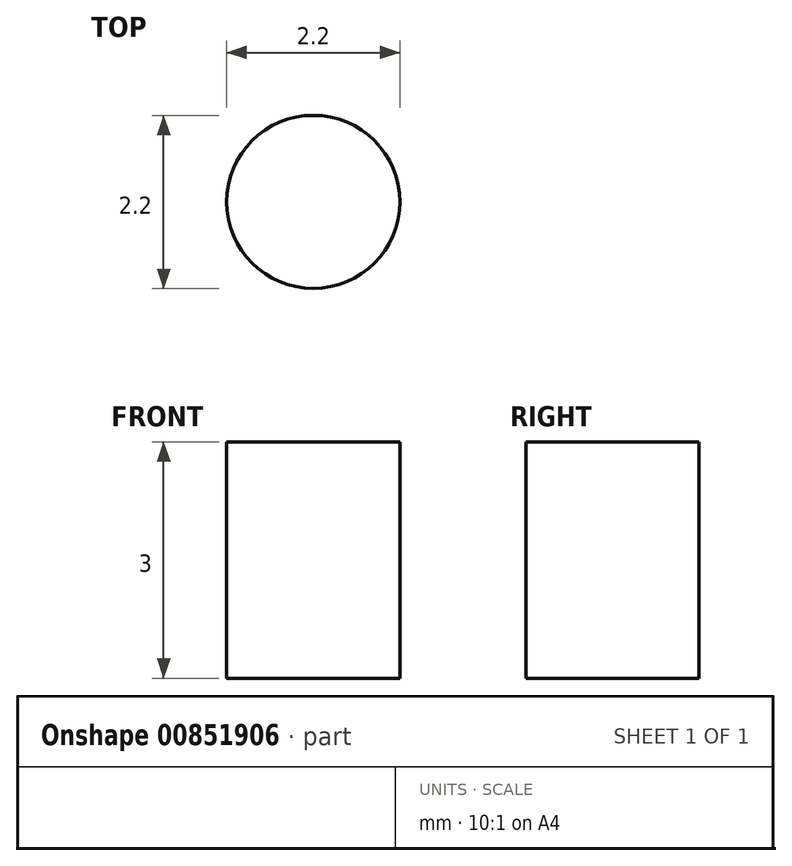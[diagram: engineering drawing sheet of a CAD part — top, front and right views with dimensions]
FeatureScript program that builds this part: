
annotation { "Feature Type Name" : "Feature", "Feature Type Description" : "" }
export const myFeature = defineFeature(function(context is Context, id is Id, definition is map)
    precondition{}
    {
        {
            var Q0;
            Q0=qCreatedBy(makeId("Top.planeOp"),FACE);
            var sketch = newSketch(context, id + "F0", { "sketchPlane" : qUnion([Q0])});
            skLineSegment(sketch, "E0.bottom", {"start": v(0, 0) * mm, "end": v(297, 0) * mm, "construction": true});
            skLineSegment(sketch, "E0.top", {"start": v(0, 210) * mm, "end": v(297, 210) * mm, "construction": true});
            skLineSegment(sketch, "E0.left", {"start": v(0, 0) * mm, "end": v(0, 210) * mm, "construction": true});
            skLineSegment(sketch, "E0.right", {"start": v(297, 0) * mm, "end": v(297, 210) * mm, "construction": true});
            skCircle(sketch, "E1.MirrorC", {"center": v(268.86, 107.9) * mm, "radius": 1.1 * mm});
            skCircle(sketch, "E2.MirrorC", {"center": v(181.7, 17) * mm, "radius": 1.1 * mm});
            skCircle(sketch, "E3.MirrorC", {"center": v(31.1, 63.5) * mm, "radius": 1.1 * mm});
            skCircle(sketch, "E4.MirrorC", {"center": v(270.3, 149.4) * mm, "radius": 1.1 * mm});
            skCircle(sketch, "E5.MirrorC", {"center": v(179.5, 167.6) * mm, "radius": 1.1 * mm});
            skCircle(sketch, "E6.MirrorC", {"center": v(35.2, 173) * mm, "radius": 1.1 * mm});
            skCircle(sketch, "E7.MirrorC", {"center": v(132.2, 155.5) * mm, "radius": 1.1 * mm});
            skCircle(sketch, "E8.MirrorC", {"center": v(132.2, 92.5) * mm, "radius": 1.1 * mm});
            skCircle(sketch, "E9.MirrorC", {"center": v(31.1, 100) * mm, "radius": 1.1 * mm});
            skCircle(sketch, "E10.MirrorC", {"center": v(85.7, 17) * mm, "radius": 1.1 * mm});
            skCircle(sketch, "E11.MirrorC", {"center": v(24.2, 17) * mm, "radius": 1.1 * mm});
            skLineSegment(sketch, "E12.MirrorCS", {"start": v(293, 190) * mm, "end": v(293, 6) * mm});
            skLineSegment(sketch, "E13.MirrorCS", {"start": v(292, 5) * mm, "end": v(6, 5) * mm});
            skLineSegment(sketch, "E14.MirrorCS", {"start": v(5, 6) * mm, "end": v(5, 190) * mm});
            skLineSegment(sketch, "E15.MirrorCS", {"start": v(6, 191) * mm, "end": v(292, 191) * mm});
            skLineSegment(sketch, "E16.bottom", {"start": v(18, 11) * mm, "end": v(28, 11) * mm});
            skLineSegment(sketch, "E16.top", {"start": v(18, 8) * mm, "end": v(28, 8) * mm});
            skLineSegment(sketch, "E16.left", {"start": v(18, 11) * mm, "end": v(18, 8) * mm});
            skLineSegment(sketch, "E16.right", {"start": v(28, 11) * mm, "end": v(28, 8) * mm});
            skLineSegment(sketch, "E17.bottom", {"start": v(102, 11) * mm, "end": v(112, 11) * mm});
            skLineSegment(sketch, "E17.top", {"start": v(102, 8) * mm, "end": v(112, 8) * mm});
            skLineSegment(sketch, "E17.left", {"start": v(102, 11) * mm, "end": v(102, 8) * mm});
            skLineSegment(sketch, "E17.right", {"start": v(112, 11) * mm, "end": v(112, 8) * mm});
            skLineSegment(sketch, "E18.bottom", {"start": v(8, 28) * mm, "end": v(11, 28) * mm});
            skLineSegment(sketch, "E18.top", {"start": v(8, 18) * mm, "end": v(11, 18) * mm});
            skLineSegment(sketch, "E18.left", {"start": v(8, 28) * mm, "end": v(8, 18) * mm});
            skLineSegment(sketch, "E18.right", {"start": v(11, 28) * mm, "end": v(11, 18) * mm});
            skLineSegment(sketch, "E19.bottom", {"start": v(8, 103) * mm, "end": v(11, 103) * mm});
            skLineSegment(sketch, "E19.top", {"start": v(8, 93) * mm, "end": v(11, 93) * mm});
            skLineSegment(sketch, "E19.left", {"start": v(8, 103) * mm, "end": v(8, 93) * mm});
            skLineSegment(sketch, "E19.right", {"start": v(11, 103) * mm, "end": v(11, 93) * mm});
            skLineSegment(sketch, "E20", {"start": v(149, 5) * mm, "end": v(149, 191) * mm, "construction": true});
            skLineSegment(sketch, "E21", {"start": v(5, 98) * mm, "end": v(293, 98) * mm, "construction": true});
            skLineSegment(sketch, "E22.MirrorCS", {"start": v(196, 11) * mm, "end": v(186, 11) * mm});
            skLineSegment(sketch, "E23.MirrorCS", {"start": v(196, 8) * mm, "end": v(186, 8) * mm});
            skLineSegment(sketch, "E24.MirrorCS", {"start": v(196, 11) * mm, "end": v(196, 8) * mm});
            skLineSegment(sketch, "E25.MirrorCS", {"start": v(186, 11) * mm, "end": v(186, 8) * mm});
            skLineSegment(sketch, "E26.MirrorCS", {"start": v(270, 11) * mm, "end": v(270, 8) * mm});
            skLineSegment(sketch, "E27.MirrorCS", {"start": v(280, 11) * mm, "end": v(280, 8) * mm});
            skLineSegment(sketch, "E28.MirrorCS", {"start": v(280, 8) * mm, "end": v(270, 8) * mm});
            skLineSegment(sketch, "E29.MirrorCS", {"start": v(280, 11) * mm, "end": v(270, 11) * mm});
            skLineSegment(sketch, "E30.MirrorCS", {"start": v(287, 28) * mm, "end": v(287, 18) * mm});
            skLineSegment(sketch, "E31.MirrorCS", {"start": v(290, 18) * mm, "end": v(287, 18) * mm});
            skLineSegment(sketch, "E32.MirrorCS", {"start": v(290, 28) * mm, "end": v(287, 28) * mm});
            skLineSegment(sketch, "E33.MirrorCS", {"start": v(290, 28) * mm, "end": v(290, 18) * mm});
            skLineSegment(sketch, "E34.MirrorCS", {"start": v(290, 103) * mm, "end": v(287, 103) * mm});
            skLineSegment(sketch, "E35.MirrorCS", {"start": v(287, 103) * mm, "end": v(287, 93) * mm});
            skLineSegment(sketch, "E36.MirrorCS", {"start": v(290, 103) * mm, "end": v(290, 93) * mm});
            skLineSegment(sketch, "E37.MirrorCS", {"start": v(290, 93) * mm, "end": v(287, 93) * mm});
            skLineSegment(sketch, "E38.MirrorCS", {"start": v(8, 168) * mm, "end": v(8, 178) * mm});
            skLineSegment(sketch, "E39.MirrorCS", {"start": v(8, 178) * mm, "end": v(11, 178) * mm});
            skLineSegment(sketch, "E40.MirrorCS", {"start": v(8, 168) * mm, "end": v(11, 168) * mm});
            skLineSegment(sketch, "E41.MirrorCS", {"start": v(11, 168) * mm, "end": v(11, 178) * mm});
            skLineSegment(sketch, "E42.MirrorCS", {"start": v(28, 185) * mm, "end": v(28, 188) * mm});
            skLineSegment(sketch, "E43.MirrorCS", {"start": v(18, 185) * mm, "end": v(18, 188) * mm});
            skLineSegment(sketch, "E44.MirrorCS", {"start": v(18, 188) * mm, "end": v(28, 188) * mm});
            skLineSegment(sketch, "E45.MirrorCS", {"start": v(18, 185) * mm, "end": v(28, 185) * mm});
            skLineSegment(sketch, "E46.MirrorCS", {"start": v(102, 185) * mm, "end": v(112, 185) * mm});
            skLineSegment(sketch, "E47.MirrorCS", {"start": v(102, 185) * mm, "end": v(102, 188) * mm});
            skLineSegment(sketch, "E48.MirrorCS", {"start": v(112, 185) * mm, "end": v(112, 188) * mm});
            skLineSegment(sketch, "E49.MirrorCS", {"start": v(102, 188) * mm, "end": v(112, 188) * mm});
            skLineSegment(sketch, "E50.MirrorCS", {"start": v(196, 185) * mm, "end": v(186, 185) * mm});
            skLineSegment(sketch, "E51.MirrorCS", {"start": v(196, 188) * mm, "end": v(186, 188) * mm});
            skLineSegment(sketch, "E52.MirrorCS", {"start": v(186, 185) * mm, "end": v(186, 188) * mm});
            skLineSegment(sketch, "E53.MirrorCS", {"start": v(196, 185) * mm, "end": v(196, 188) * mm});
            skLineSegment(sketch, "E54.MirrorCS", {"start": v(280, 185) * mm, "end": v(280, 188) * mm});
            skLineSegment(sketch, "E55.MirrorCS", {"start": v(280, 185) * mm, "end": v(270, 185) * mm});
            skLineSegment(sketch, "E56.MirrorCS", {"start": v(280, 188) * mm, "end": v(270, 188) * mm});
            skLineSegment(sketch, "E57.MirrorCS", {"start": v(270, 185) * mm, "end": v(270, 188) * mm});
            skLineSegment(sketch, "E58.MirrorCS", {"start": v(290, 178) * mm, "end": v(287, 178) * mm});
            skLineSegment(sketch, "E59.MirrorCS", {"start": v(290, 168) * mm, "end": v(290, 178) * mm});
            skLineSegment(sketch, "E60.MirrorCS", {"start": v(287, 168) * mm, "end": v(287, 178) * mm});
            skLineSegment(sketch, "E61.MirrorCS", {"start": v(290, 168) * mm, "end": v(287, 168) * mm});
            skLineSegment(sketch, "E62", {"start": v(42.5, 32.5) * mm, "end": v(57.5, 32.5) * mm, "construction": true});
            skArc(sketch, "E63.0.startCap", {"start": v(42.5, 31) * mm, "mid": v(41, 32.5) * mm, "end": v(42.5, 34) * mm});
            skArc(sketch, "E63.0.endCap", {"start": v(57.5, 34) * mm, "mid": v(59, 32.5) * mm, "end": v(57.5, 31) * mm});
            skLineSegment(sketch, "E63.0.left", {"start": v(42.5, 34) * mm, "end": v(57.5, 34) * mm});
            skLineSegment(sketch, "E63.0.right", {"start": v(42.5, 31) * mm, "end": v(57.5, 31) * mm});
            skLineSegment(sketch, "E64.0.1.0", {"start": v(42.5, 56) * mm, "end": v(57.5, 56) * mm});
            skLineSegment(sketch, "E64.0.1.1", {"start": v(42.5, 59) * mm, "end": v(57.5, 59) * mm});
            skArc(sketch, "E64.0.1.2", {"start": v(42.5, 56) * mm, "mid": v(41, 57.5) * mm, "end": v(42.5, 59) * mm});
            skArc(sketch, "E64.0.1.3", {"start": v(57.5, 59) * mm, "mid": v(59, 57.5) * mm, "end": v(57.5, 56) * mm});
            skLineSegment(sketch, "E64.0.2.0", {"start": v(42.5, 81) * mm, "end": v(57.5, 81) * mm});
            skLineSegment(sketch, "E64.0.2.1", {"start": v(42.5, 84) * mm, "end": v(57.5, 84) * mm});
            skArc(sketch, "E64.0.2.2", {"start": v(42.5, 81) * mm, "mid": v(41, 82.5) * mm, "end": v(42.5, 84) * mm});
            skArc(sketch, "E64.0.2.3", {"start": v(57.5, 84) * mm, "mid": v(59, 82.5) * mm, "end": v(57.5, 81) * mm});
            skLineSegment(sketch, "E64.0.3.0", {"start": v(42.5, 106) * mm, "end": v(57.5, 106) * mm});
            skLineSegment(sketch, "E64.0.3.1", {"start": v(42.5, 109) * mm, "end": v(57.5, 109) * mm});
            skArc(sketch, "E64.0.3.2", {"start": v(42.5, 106) * mm, "mid": v(41, 107.5) * mm, "end": v(42.5, 109) * mm});
            skArc(sketch, "E64.0.3.3", {"start": v(57.5, 109) * mm, "mid": v(59, 107.5) * mm, "end": v(57.5, 106) * mm});
            skLineSegment(sketch, "E64.0.4.0", {"start": v(42.5, 131) * mm, "end": v(57.5, 131) * mm});
            skLineSegment(sketch, "E64.0.4.1", {"start": v(42.5, 134) * mm, "end": v(57.5, 134) * mm});
            skArc(sketch, "E64.0.4.2", {"start": v(42.5, 131) * mm, "mid": v(41, 132.5) * mm, "end": v(42.5, 134) * mm});
            skArc(sketch, "E64.0.4.3", {"start": v(57.5, 134) * mm, "mid": v(59, 132.5) * mm, "end": v(57.5, 131) * mm});
            skLineSegment(sketch, "E64.0.5.0", {"start": v(42.5, 156) * mm, "end": v(57.5, 156) * mm});
            skLineSegment(sketch, "E64.0.5.1", {"start": v(42.5, 159) * mm, "end": v(57.5, 159) * mm});
            skArc(sketch, "E64.0.5.2", {"start": v(42.5, 156) * mm, "mid": v(41, 157.5) * mm, "end": v(42.5, 159) * mm});
            skArc(sketch, "E64.0.5.3", {"start": v(57.5, 159) * mm, "mid": v(59, 157.5) * mm, "end": v(57.5, 156) * mm});
            skLineSegment(sketch, "E64.1.0.0", {"start": v(64.5, 31) * mm, "end": v(79.5, 31) * mm});
            skLineSegment(sketch, "E64.1.0.1", {"start": v(64.5, 34) * mm, "end": v(79.5, 34) * mm});
            skArc(sketch, "E64.1.0.2", {"start": v(64.5, 31) * mm, "mid": v(63, 32.5) * mm, "end": v(64.5, 34) * mm});
            skArc(sketch, "E64.1.0.3", {"start": v(79.5, 34) * mm, "mid": v(81, 32.5) * mm, "end": v(79.5, 31) * mm});
            skLineSegment(sketch, "E64.1.1.0", {"start": v(64.5, 56) * mm, "end": v(79.5, 56) * mm});
            skLineSegment(sketch, "E64.1.1.1", {"start": v(64.5, 59) * mm, "end": v(79.5, 59) * mm});
            skArc(sketch, "E64.1.1.2", {"start": v(64.5, 56) * mm, "mid": v(63, 57.5) * mm, "end": v(64.5, 59) * mm});
            skArc(sketch, "E64.1.1.3", {"start": v(79.5, 59) * mm, "mid": v(81, 57.5) * mm, "end": v(79.5, 56) * mm});
            skLineSegment(sketch, "E64.1.2.0", {"start": v(64.5, 81) * mm, "end": v(79.5, 81) * mm});
            skLineSegment(sketch, "E64.1.2.1", {"start": v(64.5, 84) * mm, "end": v(79.5, 84) * mm});
            skArc(sketch, "E64.1.2.2", {"start": v(64.5, 81) * mm, "mid": v(63, 82.5) * mm, "end": v(64.5, 84) * mm});
            skArc(sketch, "E64.1.2.3", {"start": v(79.5, 84) * mm, "mid": v(81, 82.5) * mm, "end": v(79.5, 81) * mm});
            skLineSegment(sketch, "E64.1.3.0", {"start": v(64.5, 106) * mm, "end": v(79.5, 106) * mm});
            skLineSegment(sketch, "E64.1.3.1", {"start": v(64.5, 109) * mm, "end": v(79.5, 109) * mm});
            skArc(sketch, "E64.1.3.2", {"start": v(64.5, 106) * mm, "mid": v(63, 107.5) * mm, "end": v(64.5, 109) * mm});
            skArc(sketch, "E64.1.3.3", {"start": v(79.5, 109) * mm, "mid": v(81, 107.5) * mm, "end": v(79.5, 106) * mm});
            skLineSegment(sketch, "E64.1.4.0", {"start": v(64.5, 131) * mm, "end": v(79.5, 131) * mm});
            skLineSegment(sketch, "E64.1.4.1", {"start": v(64.5, 134) * mm, "end": v(79.5, 134) * mm});
            skArc(sketch, "E64.1.4.2", {"start": v(64.5, 131) * mm, "mid": v(63, 132.5) * mm, "end": v(64.5, 134) * mm});
            skArc(sketch, "E64.1.4.3", {"start": v(79.5, 134) * mm, "mid": v(81, 132.5) * mm, "end": v(79.5, 131) * mm});
            skLineSegment(sketch, "E64.1.5.0", {"start": v(64.5, 156) * mm, "end": v(79.5, 156) * mm});
            skLineSegment(sketch, "E64.1.5.1", {"start": v(64.5, 159) * mm, "end": v(79.5, 159) * mm});
            skArc(sketch, "E64.1.5.2", {"start": v(64.5, 156) * mm, "mid": v(63, 157.5) * mm, "end": v(64.5, 159) * mm});
            skArc(sketch, "E64.1.5.3", {"start": v(79.5, 159) * mm, "mid": v(81, 157.5) * mm, "end": v(79.5, 156) * mm});
            skLineSegment(sketch, "E64.2.0.0", {"start": v(86.5, 31) * mm, "end": v(101.5, 31) * mm});
            skLineSegment(sketch, "E64.2.0.1", {"start": v(86.5, 34) * mm, "end": v(101.5, 34) * mm});
            skArc(sketch, "E64.2.0.2", {"start": v(86.5, 31) * mm, "mid": v(85, 32.5) * mm, "end": v(86.5, 34) * mm});
            skArc(sketch, "E64.2.0.3", {"start": v(101.5, 34) * mm, "mid": v(103, 32.5) * mm, "end": v(101.5, 31) * mm});
            skLineSegment(sketch, "E64.2.1.0", {"start": v(86.5, 56) * mm, "end": v(101.5, 56) * mm});
            skLineSegment(sketch, "E64.2.1.1", {"start": v(86.5, 59) * mm, "end": v(101.5, 59) * mm});
            skArc(sketch, "E64.2.1.2", {"start": v(86.5, 56) * mm, "mid": v(85, 57.5) * mm, "end": v(86.5, 59) * mm});
            skArc(sketch, "E64.2.1.3", {"start": v(101.5, 59) * mm, "mid": v(103, 57.5) * mm, "end": v(101.5, 56) * mm});
            skLineSegment(sketch, "E64.2.2.0", {"start": v(86.5, 81) * mm, "end": v(101.5, 81) * mm});
            skLineSegment(sketch, "E64.2.2.1", {"start": v(86.5, 84) * mm, "end": v(101.5, 84) * mm});
            skArc(sketch, "E64.2.2.2", {"start": v(86.5, 81) * mm, "mid": v(85, 82.5) * mm, "end": v(86.5, 84) * mm});
            skArc(sketch, "E64.2.2.3", {"start": v(101.5, 84) * mm, "mid": v(103, 82.5) * mm, "end": v(101.5, 81) * mm});
            skLineSegment(sketch, "E64.2.3.0", {"start": v(86.5, 106) * mm, "end": v(101.5, 106) * mm});
            skLineSegment(sketch, "E64.2.3.1", {"start": v(86.5, 109) * mm, "end": v(101.5, 109) * mm});
            skArc(sketch, "E64.2.3.2", {"start": v(86.5, 106) * mm, "mid": v(85, 107.5) * mm, "end": v(86.5, 109) * mm});
            skArc(sketch, "E64.2.3.3", {"start": v(101.5, 109) * mm, "mid": v(103, 107.5) * mm, "end": v(101.5, 106) * mm});
            skLineSegment(sketch, "E64.2.4.0", {"start": v(86.5, 131) * mm, "end": v(101.5, 131) * mm});
            skLineSegment(sketch, "E64.2.4.1", {"start": v(86.5, 134) * mm, "end": v(101.5, 134) * mm});
            skArc(sketch, "E64.2.4.2", {"start": v(86.5, 131) * mm, "mid": v(85, 132.5) * mm, "end": v(86.5, 134) * mm});
            skArc(sketch, "E64.2.4.3", {"start": v(101.5, 134) * mm, "mid": v(103, 132.5) * mm, "end": v(101.5, 131) * mm});
            skLineSegment(sketch, "E64.2.5.0", {"start": v(86.5, 156) * mm, "end": v(101.5, 156) * mm});
            skLineSegment(sketch, "E64.2.5.1", {"start": v(86.5, 159) * mm, "end": v(101.5, 159) * mm});
            skArc(sketch, "E64.2.5.2", {"start": v(86.5, 156) * mm, "mid": v(85, 157.5) * mm, "end": v(86.5, 159) * mm});
            skArc(sketch, "E64.2.5.3", {"start": v(101.5, 159) * mm, "mid": v(103, 157.5) * mm, "end": v(101.5, 156) * mm});
            skLineSegment(sketch, "E64.3.0.0", {"start": v(108.5, 31) * mm, "end": v(123.5, 31) * mm});
            skLineSegment(sketch, "E64.3.0.1", {"start": v(108.5, 34) * mm, "end": v(123.5, 34) * mm});
            skArc(sketch, "E64.3.0.2", {"start": v(108.5, 31) * mm, "mid": v(107, 32.5) * mm, "end": v(108.5, 34) * mm});
            skArc(sketch, "E64.3.0.3", {"start": v(123.5, 34) * mm, "mid": v(125, 32.5) * mm, "end": v(123.5, 31) * mm});
            skLineSegment(sketch, "E64.3.1.0", {"start": v(108.5, 56) * mm, "end": v(123.5, 56) * mm});
            skLineSegment(sketch, "E64.3.1.1", {"start": v(108.5, 59) * mm, "end": v(123.5, 59) * mm});
            skArc(sketch, "E64.3.1.2", {"start": v(108.5, 56) * mm, "mid": v(107, 57.5) * mm, "end": v(108.5, 59) * mm});
            skArc(sketch, "E64.3.1.3", {"start": v(123.5, 59) * mm, "mid": v(125, 57.5) * mm, "end": v(123.5, 56) * mm});
            skLineSegment(sketch, "E64.3.2.0", {"start": v(108.5, 81) * mm, "end": v(123.5, 81) * mm});
            skLineSegment(sketch, "E64.3.2.1", {"start": v(108.5, 84) * mm, "end": v(123.5, 84) * mm});
            skArc(sketch, "E64.3.2.2", {"start": v(108.5, 81) * mm, "mid": v(107, 82.5) * mm, "end": v(108.5, 84) * mm});
            skArc(sketch, "E64.3.2.3", {"start": v(123.5, 84) * mm, "mid": v(125, 82.5) * mm, "end": v(123.5, 81) * mm});
            skLineSegment(sketch, "E64.3.3.0", {"start": v(108.5, 106) * mm, "end": v(123.5, 106) * mm});
            skLineSegment(sketch, "E64.3.3.1", {"start": v(108.5, 109) * mm, "end": v(123.5, 109) * mm});
            skArc(sketch, "E64.3.3.2", {"start": v(108.5, 106) * mm, "mid": v(107, 107.5) * mm, "end": v(108.5, 109) * mm});
            skArc(sketch, "E64.3.3.3", {"start": v(123.5, 109) * mm, "mid": v(125, 107.5) * mm, "end": v(123.5, 106) * mm});
            skLineSegment(sketch, "E64.3.4.0", {"start": v(108.5, 131) * mm, "end": v(123.5, 131) * mm});
            skLineSegment(sketch, "E64.3.4.1", {"start": v(108.5, 134) * mm, "end": v(123.5, 134) * mm});
            skArc(sketch, "E64.3.4.2", {"start": v(108.5, 131) * mm, "mid": v(107, 132.5) * mm, "end": v(108.5, 134) * mm});
            skArc(sketch, "E64.3.4.3", {"start": v(123.5, 134) * mm, "mid": v(125, 132.5) * mm, "end": v(123.5, 131) * mm});
            skLineSegment(sketch, "E64.3.5.0", {"start": v(108.5, 156) * mm, "end": v(123.5, 156) * mm});
            skLineSegment(sketch, "E64.3.5.1", {"start": v(108.5, 159) * mm, "end": v(123.5, 159) * mm});
            skArc(sketch, "E64.3.5.2", {"start": v(108.5, 156) * mm, "mid": v(107, 157.5) * mm, "end": v(108.5, 159) * mm});
            skArc(sketch, "E64.3.5.3", {"start": v(123.5, 159) * mm, "mid": v(125, 157.5) * mm, "end": v(123.5, 156) * mm});
            skLineSegment(sketch, "E64.4.0.0", {"start": v(130.5, 31) * mm, "end": v(145.5, 31) * mm});
            skLineSegment(sketch, "E64.4.0.1", {"start": v(130.5, 34) * mm, "end": v(145.5, 34) * mm});
            skArc(sketch, "E64.4.0.2", {"start": v(130.5, 31) * mm, "mid": v(129, 32.5) * mm, "end": v(130.5, 34) * mm});
            skArc(sketch, "E64.4.0.3", {"start": v(145.5, 34) * mm, "mid": v(147, 32.5) * mm, "end": v(145.5, 31) * mm});
            skLineSegment(sketch, "E64.4.1.0", {"start": v(130.5, 56) * mm, "end": v(145.5, 56) * mm});
            skLineSegment(sketch, "E64.4.1.1", {"start": v(130.5, 59) * mm, "end": v(145.5, 59) * mm});
            skArc(sketch, "E64.4.1.2", {"start": v(130.5, 56) * mm, "mid": v(129, 57.5) * mm, "end": v(130.5, 59) * mm});
            skArc(sketch, "E64.4.1.3", {"start": v(145.5, 59) * mm, "mid": v(147, 57.5) * mm, "end": v(145.5, 56) * mm});
            skLineSegment(sketch, "E64.4.2.0", {"start": v(130.5, 81) * mm, "end": v(145.5, 81) * mm});
            skLineSegment(sketch, "E64.4.2.1", {"start": v(130.5, 84) * mm, "end": v(145.5, 84) * mm});
            skArc(sketch, "E64.4.2.2", {"start": v(130.5, 81) * mm, "mid": v(129, 82.5) * mm, "end": v(130.5, 84) * mm});
            skArc(sketch, "E64.4.2.3", {"start": v(145.5, 84) * mm, "mid": v(147, 82.5) * mm, "end": v(145.5, 81) * mm});
            skLineSegment(sketch, "E64.4.3.0", {"start": v(130.5, 106) * mm, "end": v(145.5, 106) * mm});
            skLineSegment(sketch, "E64.4.3.1", {"start": v(130.5, 109) * mm, "end": v(145.5, 109) * mm});
            skArc(sketch, "E64.4.3.2", {"start": v(130.5, 106) * mm, "mid": v(129, 107.5) * mm, "end": v(130.5, 109) * mm});
            skArc(sketch, "E64.4.3.3", {"start": v(145.5, 109) * mm, "mid": v(147, 107.5) * mm, "end": v(145.5, 106) * mm});
            skLineSegment(sketch, "E64.4.4.0", {"start": v(130.5, 131) * mm, "end": v(145.5, 131) * mm});
            skLineSegment(sketch, "E64.4.4.1", {"start": v(130.5, 134) * mm, "end": v(145.5, 134) * mm});
            skArc(sketch, "E64.4.4.2", {"start": v(130.5, 131) * mm, "mid": v(129, 132.5) * mm, "end": v(130.5, 134) * mm});
            skArc(sketch, "E64.4.4.3", {"start": v(145.5, 134) * mm, "mid": v(147, 132.5) * mm, "end": v(145.5, 131) * mm});
            skLineSegment(sketch, "E64.5.0.0", {"start": v(152.5, 31) * mm, "end": v(167.5, 31) * mm});
            skLineSegment(sketch, "E64.5.0.1", {"start": v(152.5, 34) * mm, "end": v(167.5, 34) * mm});
            skArc(sketch, "E64.5.0.2", {"start": v(152.5, 31) * mm, "mid": v(151, 32.5) * mm, "end": v(152.5, 34) * mm});
            skArc(sketch, "E64.5.0.3", {"start": v(167.5, 34) * mm, "mid": v(169, 32.5) * mm, "end": v(167.5, 31) * mm});
            skLineSegment(sketch, "E64.5.1.0", {"start": v(152.5, 56) * mm, "end": v(167.5, 56) * mm});
            skLineSegment(sketch, "E64.5.1.1", {"start": v(152.5, 59) * mm, "end": v(167.5, 59) * mm});
            skArc(sketch, "E64.5.1.2", {"start": v(152.5, 56) * mm, "mid": v(151, 57.5) * mm, "end": v(152.5, 59) * mm});
            skArc(sketch, "E64.5.1.3", {"start": v(167.5, 59) * mm, "mid": v(169, 57.5) * mm, "end": v(167.5, 56) * mm});
            skLineSegment(sketch, "E64.5.2.0", {"start": v(152.5, 81) * mm, "end": v(167.5, 81) * mm});
            skLineSegment(sketch, "E64.5.2.1", {"start": v(152.5, 84) * mm, "end": v(167.5, 84) * mm});
            skArc(sketch, "E64.5.2.2", {"start": v(152.5, 81) * mm, "mid": v(151, 82.5) * mm, "end": v(152.5, 84) * mm});
            skArc(sketch, "E64.5.2.3", {"start": v(167.5, 84) * mm, "mid": v(169, 82.5) * mm, "end": v(167.5, 81) * mm});
            skLineSegment(sketch, "E64.5.3.0", {"start": v(152.5, 106) * mm, "end": v(167.5, 106) * mm});
            skLineSegment(sketch, "E64.5.3.1", {"start": v(152.5, 109) * mm, "end": v(167.5, 109) * mm});
            skArc(sketch, "E64.5.3.2", {"start": v(152.5, 106) * mm, "mid": v(151, 107.5) * mm, "end": v(152.5, 109) * mm});
            skArc(sketch, "E64.5.3.3", {"start": v(167.5, 109) * mm, "mid": v(169, 107.5) * mm, "end": v(167.5, 106) * mm});
            skLineSegment(sketch, "E64.5.4.0", {"start": v(152.5, 131) * mm, "end": v(167.5, 131) * mm});
            skLineSegment(sketch, "E64.5.4.1", {"start": v(152.5, 134) * mm, "end": v(167.5, 134) * mm});
            skArc(sketch, "E64.5.4.2", {"start": v(152.5, 131) * mm, "mid": v(151, 132.5) * mm, "end": v(152.5, 134) * mm});
            skArc(sketch, "E64.5.4.3", {"start": v(167.5, 134) * mm, "mid": v(169, 132.5) * mm, "end": v(167.5, 131) * mm});
            skLineSegment(sketch, "E64.5.5.0", {"start": v(152.5, 156) * mm, "end": v(167.5, 156) * mm});
            skLineSegment(sketch, "E64.5.5.1", {"start": v(152.5, 159) * mm, "end": v(167.5, 159) * mm});
            skArc(sketch, "E64.5.5.2", {"start": v(152.5, 156) * mm, "mid": v(151, 157.5) * mm, "end": v(152.5, 159) * mm});
            skArc(sketch, "E64.5.5.3", {"start": v(167.5, 159) * mm, "mid": v(169, 157.5) * mm, "end": v(167.5, 156) * mm});
            skLineSegment(sketch, "E64.6.0.0", {"start": v(174.5, 31) * mm, "end": v(189.5, 31) * mm});
            skLineSegment(sketch, "E64.6.0.1", {"start": v(174.5, 34) * mm, "end": v(189.5, 34) * mm});
            skArc(sketch, "E64.6.0.2", {"start": v(174.5, 31) * mm, "mid": v(173, 32.5) * mm, "end": v(174.5, 34) * mm});
            skArc(sketch, "E64.6.0.3", {"start": v(189.5, 34) * mm, "mid": v(191, 32.5) * mm, "end": v(189.5, 31) * mm});
            skLineSegment(sketch, "E64.6.1.0", {"start": v(174.5, 56) * mm, "end": v(189.5, 56) * mm});
            skLineSegment(sketch, "E64.6.1.1", {"start": v(174.5, 59) * mm, "end": v(189.5, 59) * mm});
            skArc(sketch, "E64.6.1.2", {"start": v(174.5, 56) * mm, "mid": v(173, 57.5) * mm, "end": v(174.5, 59) * mm});
            skArc(sketch, "E64.6.1.3", {"start": v(189.5, 59) * mm, "mid": v(191, 57.5) * mm, "end": v(189.5, 56) * mm});
            skLineSegment(sketch, "E64.6.2.0", {"start": v(174.5, 81) * mm, "end": v(189.5, 81) * mm});
            skLineSegment(sketch, "E64.6.2.1", {"start": v(174.5, 84) * mm, "end": v(189.5, 84) * mm});
            skArc(sketch, "E64.6.2.2", {"start": v(174.5, 81) * mm, "mid": v(173, 82.5) * mm, "end": v(174.5, 84) * mm});
            skArc(sketch, "E64.6.2.3", {"start": v(189.5, 84) * mm, "mid": v(191, 82.5) * mm, "end": v(189.5, 81) * mm});
            skLineSegment(sketch, "E64.6.3.0", {"start": v(174.5, 106) * mm, "end": v(189.5, 106) * mm});
            skLineSegment(sketch, "E64.6.3.1", {"start": v(174.5, 109) * mm, "end": v(189.5, 109) * mm});
            skArc(sketch, "E64.6.3.2", {"start": v(174.5, 106) * mm, "mid": v(173, 107.5) * mm, "end": v(174.5, 109) * mm});
            skArc(sketch, "E64.6.3.3", {"start": v(189.5, 109) * mm, "mid": v(191, 107.5) * mm, "end": v(189.5, 106) * mm});
            skLineSegment(sketch, "E64.6.4.0", {"start": v(174.5, 131) * mm, "end": v(189.5, 131) * mm});
            skLineSegment(sketch, "E64.6.4.1", {"start": v(174.5, 134) * mm, "end": v(189.5, 134) * mm});
            skArc(sketch, "E64.6.4.2", {"start": v(174.5, 131) * mm, "mid": v(173, 132.5) * mm, "end": v(174.5, 134) * mm});
            skArc(sketch, "E64.6.4.3", {"start": v(189.5, 134) * mm, "mid": v(191, 132.5) * mm, "end": v(189.5, 131) * mm});
            skLineSegment(sketch, "E64.6.5.0", {"start": v(174.5, 156) * mm, "end": v(189.5, 156) * mm});
            skLineSegment(sketch, "E64.6.5.1", {"start": v(174.5, 159) * mm, "end": v(189.5, 159) * mm});
            skArc(sketch, "E64.6.5.2", {"start": v(174.5, 156) * mm, "mid": v(173, 157.5) * mm, "end": v(174.5, 159) * mm});
            skArc(sketch, "E64.6.5.3", {"start": v(189.5, 159) * mm, "mid": v(191, 157.5) * mm, "end": v(189.5, 156) * mm});
            skLineSegment(sketch, "E64.7.0.0", {"start": v(196.5, 31) * mm, "end": v(211.5, 31) * mm});
            skLineSegment(sketch, "E64.7.0.1", {"start": v(196.5, 34) * mm, "end": v(211.5, 34) * mm});
            skArc(sketch, "E64.7.0.2", {"start": v(196.5, 31) * mm, "mid": v(195, 32.5) * mm, "end": v(196.5, 34) * mm});
            skArc(sketch, "E64.7.0.3", {"start": v(211.5, 34) * mm, "mid": v(213, 32.5) * mm, "end": v(211.5, 31) * mm});
            skLineSegment(sketch, "E64.7.1.0", {"start": v(196.5, 56) * mm, "end": v(211.5, 56) * mm});
            skLineSegment(sketch, "E64.7.1.1", {"start": v(196.5, 59) * mm, "end": v(211.5, 59) * mm});
            skArc(sketch, "E64.7.1.2", {"start": v(196.5, 56) * mm, "mid": v(195, 57.5) * mm, "end": v(196.5, 59) * mm});
            skArc(sketch, "E64.7.1.3", {"start": v(211.5, 59) * mm, "mid": v(213, 57.5) * mm, "end": v(211.5, 56) * mm});
            skLineSegment(sketch, "E64.7.2.0", {"start": v(196.5, 81) * mm, "end": v(211.5, 81) * mm});
            skLineSegment(sketch, "E64.7.2.1", {"start": v(196.5, 84) * mm, "end": v(211.5, 84) * mm});
            skArc(sketch, "E64.7.2.2", {"start": v(196.5, 81) * mm, "mid": v(195, 82.5) * mm, "end": v(196.5, 84) * mm});
            skArc(sketch, "E64.7.2.3", {"start": v(211.5, 84) * mm, "mid": v(213, 82.5) * mm, "end": v(211.5, 81) * mm});
            skLineSegment(sketch, "E64.7.3.0", {"start": v(196.5, 106) * mm, "end": v(211.5, 106) * mm});
            skLineSegment(sketch, "E64.7.3.1", {"start": v(196.5, 109) * mm, "end": v(211.5, 109) * mm});
            skArc(sketch, "E64.7.3.2", {"start": v(196.5, 106) * mm, "mid": v(195, 107.5) * mm, "end": v(196.5, 109) * mm});
            skArc(sketch, "E64.7.3.3", {"start": v(211.5, 109) * mm, "mid": v(213, 107.5) * mm, "end": v(211.5, 106) * mm});
            skLineSegment(sketch, "E64.7.4.0", {"start": v(196.5, 131) * mm, "end": v(211.5, 131) * mm});
            skLineSegment(sketch, "E64.7.4.1", {"start": v(196.5, 134) * mm, "end": v(211.5, 134) * mm});
            skArc(sketch, "E64.7.4.2", {"start": v(196.5, 131) * mm, "mid": v(195, 132.5) * mm, "end": v(196.5, 134) * mm});
            skArc(sketch, "E64.7.4.3", {"start": v(211.5, 134) * mm, "mid": v(213, 132.5) * mm, "end": v(211.5, 131) * mm});
            skLineSegment(sketch, "E64.7.5.0", {"start": v(196.5, 156) * mm, "end": v(211.5, 156) * mm});
            skLineSegment(sketch, "E64.7.5.1", {"start": v(196.5, 159) * mm, "end": v(211.5, 159) * mm});
            skArc(sketch, "E64.7.5.2", {"start": v(196.5, 156) * mm, "mid": v(195, 157.5) * mm, "end": v(196.5, 159) * mm});
            skArc(sketch, "E64.7.5.3", {"start": v(211.5, 159) * mm, "mid": v(213, 157.5) * mm, "end": v(211.5, 156) * mm});
            skLineSegment(sketch, "E64.8.0.0", {"start": v(218.5, 31) * mm, "end": v(233.5, 31) * mm});
            skLineSegment(sketch, "E64.8.0.1", {"start": v(218.5, 34) * mm, "end": v(233.5, 34) * mm});
            skArc(sketch, "E64.8.0.2", {"start": v(218.5, 31) * mm, "mid": v(217, 32.5) * mm, "end": v(218.5, 34) * mm});
            skArc(sketch, "E64.8.0.3", {"start": v(233.5, 34) * mm, "mid": v(235, 32.5) * mm, "end": v(233.5, 31) * mm});
            skLineSegment(sketch, "E64.8.1.0", {"start": v(218.5, 56) * mm, "end": v(233.5, 56) * mm});
            skLineSegment(sketch, "E64.8.1.1", {"start": v(218.5, 59) * mm, "end": v(233.5, 59) * mm});
            skArc(sketch, "E64.8.1.2", {"start": v(218.5, 56) * mm, "mid": v(217, 57.5) * mm, "end": v(218.5, 59) * mm});
            skArc(sketch, "E64.8.1.3", {"start": v(233.5, 59) * mm, "mid": v(235, 57.5) * mm, "end": v(233.5, 56) * mm});
            skLineSegment(sketch, "E64.8.2.0", {"start": v(218.5, 81) * mm, "end": v(233.5, 81) * mm});
            skLineSegment(sketch, "E64.8.2.1", {"start": v(218.5, 84) * mm, "end": v(233.5, 84) * mm});
            skArc(sketch, "E64.8.2.2", {"start": v(218.5, 81) * mm, "mid": v(217, 82.5) * mm, "end": v(218.5, 84) * mm});
            skArc(sketch, "E64.8.2.3", {"start": v(233.5, 84) * mm, "mid": v(235, 82.5) * mm, "end": v(233.5, 81) * mm});
            skLineSegment(sketch, "E64.8.3.0", {"start": v(218.5, 106) * mm, "end": v(233.5, 106) * mm});
            skLineSegment(sketch, "E64.8.3.1", {"start": v(218.5, 109) * mm, "end": v(233.5, 109) * mm});
            skArc(sketch, "E64.8.3.2", {"start": v(218.5, 106) * mm, "mid": v(217, 107.5) * mm, "end": v(218.5, 109) * mm});
            skArc(sketch, "E64.8.3.3", {"start": v(233.5, 109) * mm, "mid": v(235, 107.5) * mm, "end": v(233.5, 106) * mm});
            skLineSegment(sketch, "E64.8.4.0", {"start": v(218.5, 131) * mm, "end": v(233.5, 131) * mm});
            skLineSegment(sketch, "E64.8.4.1", {"start": v(218.5, 134) * mm, "end": v(233.5, 134) * mm});
            skArc(sketch, "E64.8.4.2", {"start": v(218.5, 131) * mm, "mid": v(217, 132.5) * mm, "end": v(218.5, 134) * mm});
            skArc(sketch, "E64.8.4.3", {"start": v(233.5, 134) * mm, "mid": v(235, 132.5) * mm, "end": v(233.5, 131) * mm});
            skLineSegment(sketch, "E64.8.5.0", {"start": v(218.5, 156) * mm, "end": v(233.5, 156) * mm});
            skLineSegment(sketch, "E64.8.5.1", {"start": v(218.5, 159) * mm, "end": v(233.5, 159) * mm});
            skArc(sketch, "E64.8.5.2", {"start": v(218.5, 156) * mm, "mid": v(217, 157.5) * mm, "end": v(218.5, 159) * mm});
            skArc(sketch, "E64.8.5.3", {"start": v(233.5, 159) * mm, "mid": v(235, 157.5) * mm, "end": v(233.5, 156) * mm});
            skLineSegment(sketch, "E64.9.0.0", {"start": v(240.5, 31) * mm, "end": v(255.5, 31) * mm});
            skLineSegment(sketch, "E64.9.0.1", {"start": v(240.5, 34) * mm, "end": v(255.5, 34) * mm});
            skArc(sketch, "E64.9.0.2", {"start": v(240.5, 31) * mm, "mid": v(239, 32.5) * mm, "end": v(240.5, 34) * mm});
            skArc(sketch, "E64.9.0.3", {"start": v(255.5, 34) * mm, "mid": v(257, 32.5) * mm, "end": v(255.5, 31) * mm});
            skLineSegment(sketch, "E64.9.1.0", {"start": v(240.5, 56) * mm, "end": v(255.5, 56) * mm});
            skLineSegment(sketch, "E64.9.1.1", {"start": v(240.5, 59) * mm, "end": v(255.5, 59) * mm});
            skArc(sketch, "E64.9.1.2", {"start": v(240.5, 56) * mm, "mid": v(239, 57.5) * mm, "end": v(240.5, 59) * mm});
            skArc(sketch, "E64.9.1.3", {"start": v(255.5, 59) * mm, "mid": v(257, 57.5) * mm, "end": v(255.5, 56) * mm});
            skLineSegment(sketch, "E64.9.2.0", {"start": v(240.5, 81) * mm, "end": v(255.5, 81) * mm});
            skLineSegment(sketch, "E64.9.2.1", {"start": v(240.5, 84) * mm, "end": v(255.5, 84) * mm});
            skArc(sketch, "E64.9.2.2", {"start": v(240.5, 81) * mm, "mid": v(239, 82.5) * mm, "end": v(240.5, 84) * mm});
            skArc(sketch, "E64.9.2.3", {"start": v(255.5, 84) * mm, "mid": v(257, 82.5) * mm, "end": v(255.5, 81) * mm});
            skLineSegment(sketch, "E64.9.3.0", {"start": v(240.5, 106) * mm, "end": v(255.5, 106) * mm});
            skLineSegment(sketch, "E64.9.3.1", {"start": v(240.5, 109) * mm, "end": v(255.5, 109) * mm});
            skArc(sketch, "E64.9.3.2", {"start": v(240.5, 106) * mm, "mid": v(239, 107.5) * mm, "end": v(240.5, 109) * mm});
            skArc(sketch, "E64.9.3.3", {"start": v(255.5, 109) * mm, "mid": v(257, 107.5) * mm, "end": v(255.5, 106) * mm});
            skLineSegment(sketch, "E64.9.4.0", {"start": v(240.5, 131) * mm, "end": v(255.5, 131) * mm});
            skLineSegment(sketch, "E64.9.4.1", {"start": v(240.5, 134) * mm, "end": v(255.5, 134) * mm});
            skArc(sketch, "E64.9.4.2", {"start": v(240.5, 131) * mm, "mid": v(239, 132.5) * mm, "end": v(240.5, 134) * mm});
            skArc(sketch, "E64.9.4.3", {"start": v(255.5, 134) * mm, "mid": v(257, 132.5) * mm, "end": v(255.5, 131) * mm});
            skLineSegment(sketch, "E64.9.5.0", {"start": v(240.5, 156) * mm, "end": v(255.5, 156) * mm});
            skLineSegment(sketch, "E64.9.5.1", {"start": v(240.5, 159) * mm, "end": v(255.5, 159) * mm});
            skArc(sketch, "E64.9.5.2", {"start": v(240.5, 156) * mm, "mid": v(239, 157.5) * mm, "end": v(240.5, 159) * mm});
            skArc(sketch, "E64.9.5.3", {"start": v(255.5, 159) * mm, "mid": v(257, 157.5) * mm, "end": v(255.5, 156) * mm});
            skLineSegment(sketch, "E64.direction1", {"start": v(42.5, 31) * mm, "end": v(64.5, 31) * mm, "construction": true});
            skLineSegment(sketch, "E64.direction2", {"start": v(42.5, 31) * mm, "end": v(42.5, 56) * mm, "construction": true});
            skPoint(sketch, "E65.visualSharp", {"position": v(5, 5) * mm});
            skArc(sketch, "E65.filletArc", {"start": v(5, 6) * mm, "mid": v(5.3, 5.3) * mm, "end": v(6, 5) * mm});
            skPoint(sketch, "E66.visualSharp", {"position": v(5, 191) * mm});
            skArc(sketch, "E66.filletArc", {"start": v(6, 191) * mm, "mid": v(5.3, 190.7) * mm, "end": v(5, 190) * mm});
            skPoint(sketch, "E67.visualSharp", {"position": v(293, 5) * mm});
            skArc(sketch, "E67.filletArc", {"start": v(292, 5) * mm, "mid": v(292.7, 5.3) * mm, "end": v(293, 6) * mm});
            skPoint(sketch, "E68.visualSharp", {"position": v(293, 191) * mm});
            skArc(sketch, "E68.filletArc", {"start": v(293, 190) * mm, "mid": v(292.7, 190.7) * mm, "end": v(292, 191) * mm});
            skCircle(sketch, "E69", {"center": v(157.2, 48.3) * mm, "radius": 1.1 * mm});
            skCircle(sketch, "E70", {"center": v(157.2, 124.15) * mm, "radius": 1.1 * mm});
            skCircle(sketch, "E71", {"center": v(233.8, 48.3) * mm, "radius": 1.1 * mm});
            skCircle(sketch, "E72", {"center": v(233.8, 124.15) * mm, "radius": 1.1 * mm});
            skCircle(sketch, "E73", {"center": v(14, 182) * mm, "radius": 1.1 * mm});
            skCircle(sketch, "E74", {"center": v(14, 14) * mm, "radius": 1.1 * mm});
            skCircle(sketch, "E75", {"center": v(284, 14) * mm, "radius": 1.1 * mm});
            skCircle(sketch, "E76", {"center": v(284, 182) * mm, "radius": 1.1 * mm});
            skSolve(sketch);
        }
        {
            var Q0;
            Q0=makeQuery(id+"F0.imprint","IMPRINT",FACE,{"disambiguationData":[TD([[makeQuery(id+"F0.imprint","IMPRINT",EDGE,{"derivedFrom":sQuery(id+"F0.wireOp",EDGE,"E1.MirrorC")}),1.0]])]});
            extrude(context, id + "F1", {"entities" : qUnion([Q0]), "depth" : 3 * mm, "offsetDistance" : 25 * mm});
        }
    });
